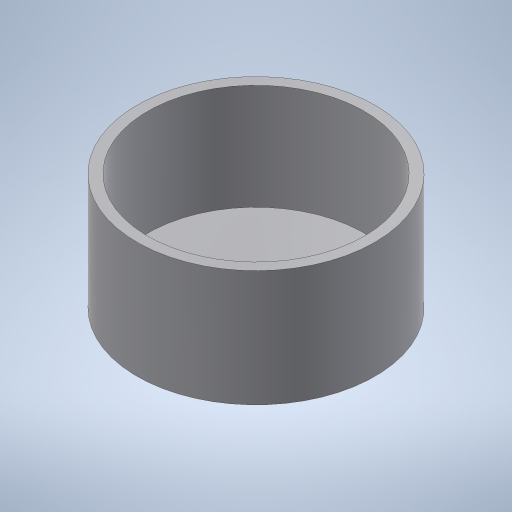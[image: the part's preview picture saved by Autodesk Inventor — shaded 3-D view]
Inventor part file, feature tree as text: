
AUTODESK INVENTOR PART (.ipt)
format: ipt  version: 2023.1 (Build 271208000, 208)  size: 212,992 bytes
history: native  units: mm
features: sketch x3, extrude x2, revolve x1, projected_geometry x1
ambient origin geometry x8: Origin, YZ Plane, XZ Plane, XY Plane, X Axis, Y Axis, Z Axis, Center Point
bodies: Solid1 (feature_tree)
feature tree (7):
  extrude  "Extrusion1"  Depth=2.0mm TaperAngle=0.0deg
  extrude  "Extrusion2"  Depth=20.0mm TaperAngle=0.0deg
  revolve  "Revolution1"  Angle=90.0deg
  sketch  "Sketch1"  dims[d0=45.0mm d1=2.0mm d2=0.0mm]
  sketch  "Sketch2"  dims[d3=2.0mm d4=20.0mm d5=0.0mm]
  projected_geometry  "Projected Loop1"
  sketch  "Sketch3"  dims[d6=5.0mm d7=90.0deg]
